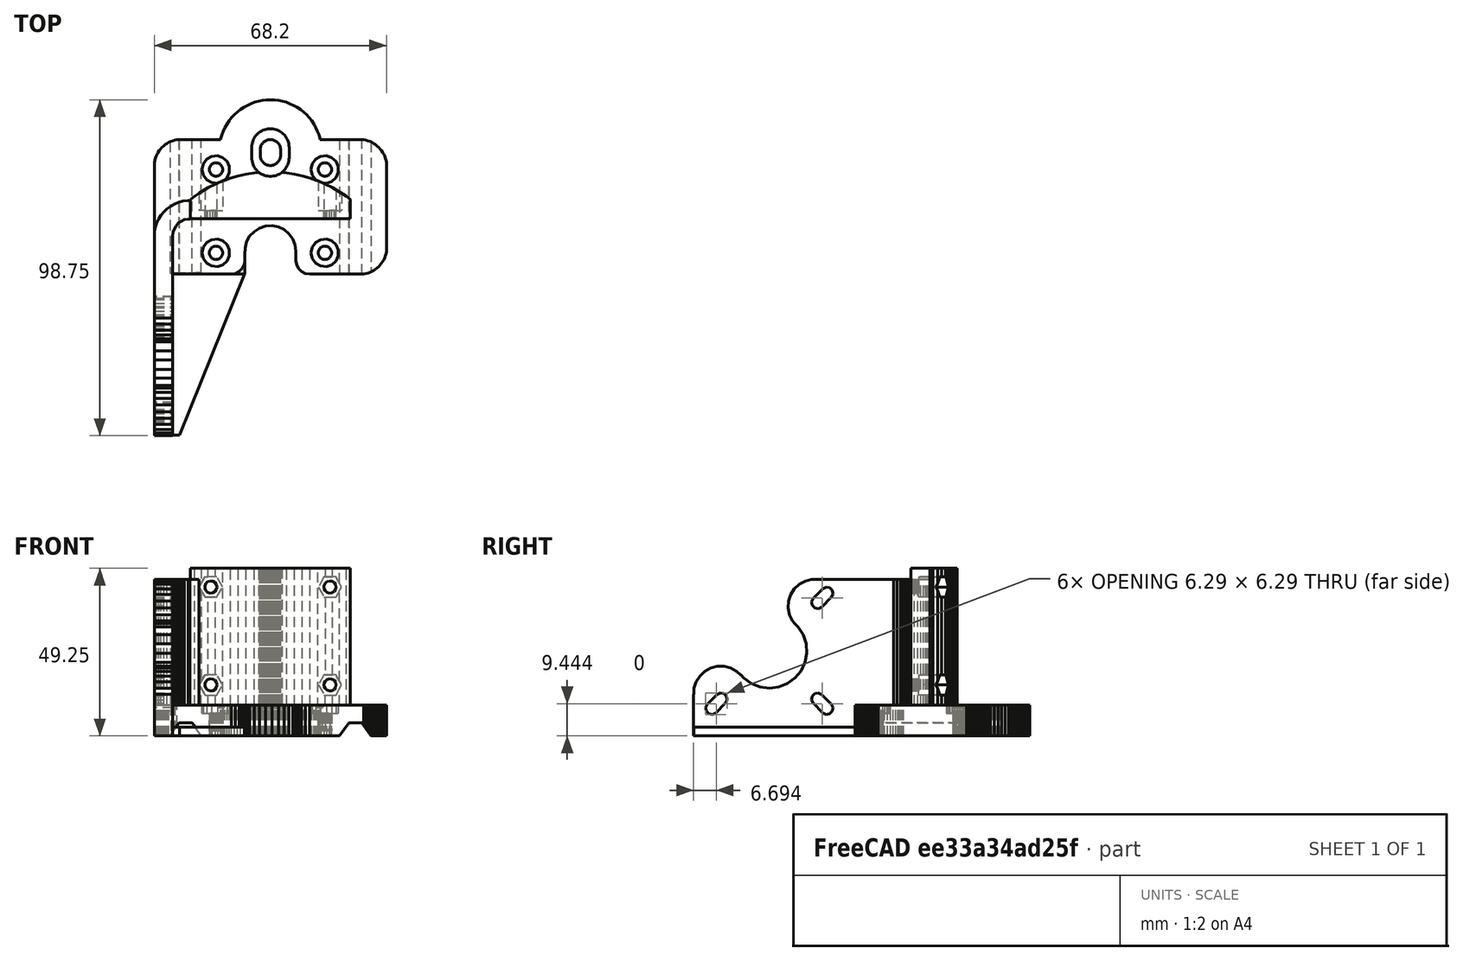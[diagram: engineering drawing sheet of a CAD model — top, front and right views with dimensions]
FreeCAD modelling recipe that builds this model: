
FCSTD DOCUMENT  (FreeCAD 0.15R4619 (Git))
Label: x_end_motor_M5
License: All rights reserved
LicenseURL: http://en.wikipedia.org/wiki/All_rights_reserved
objects: Part::Feature×1, Sketcher::SketchObject×1, PartDesign::Pad×1
note: 4 computed .brp shape members not serialized (recipe doc carries the construction recipe); baked Part::Feature solids carry a one-line shape summary decoded from their .brp

FEATURE [Part::Feature] Solid
  shape: bbox 68.2 x 98.75 x 49.25 mm, 1015 faces (baked)
FEATURE [Sketcher::SketchObject] Sketch
  ExternalGeometry = -> [Solid]
  Placement = pos=(0,0,-4.5) rot=(1,0,0;3.14159rad)
  Support = -> Solid [Face265]
  sketch-geometry (11):
    g0: LineSegment [constr] StartX=-5.5 StartY=-11.5 StartZ=0 EndX=5.5 EndY=-14.5 EndZ=0
    g1: LineSegment [constr] StartX=5.5 StartY=-11.5 StartZ=0 EndX=-5.5 EndY=-14.5 EndZ=0
    g2: LineSegment StartX=-3 StartY=-12.1818 StartZ=0 EndX=-3 EndY=-13.8182 EndZ=0
    g3: LineSegment StartX=3 StartY=-12.1818 StartZ=0 EndX=3 EndY=-13.8182 EndZ=0
    g4: LineSegment [constr] StartX=0 StartY=-12.1818 StartZ=0 EndX=0 EndY=-13 EndZ=0
    g5: LineSegment [constr] StartX=0 StartY=-13 StartZ=0 EndX=0 EndY=-13.8182 EndZ=0
    g6: LineSegment [constr] StartX=-3 StartY=-12.1818 StartZ=0 EndX=3 EndY=-12.1818 EndZ=0
    g7: LineSegment [constr] StartX=-3 StartY=-13.8182 StartZ=0 EndX=3 EndY=-13.8182 EndZ=0
    g8: ArcOfCircle CenterX=0 CenterY=-12.1818 CenterZ=0 NormalX=0 NormalY=0 NormalZ=1 Radius=3 StartAngle=0 EndAngle=3.14159
    g9: ArcOfCircle CenterX=0 CenterY=-13.8182 CenterZ=0 NormalX=0 NormalY=0 NormalZ=1 Radius=3 StartAngle=3.14159 EndAngle=6.28319
    g10: Circle CenterX=0 CenterY=-13 CenterZ=0 NormalX=0 NormalY=0 NormalZ=1 Radius=7.27781
  constraints (30):
    c: Coincident(g0,g-3)
    c: Coincident(g0,g-5)
    c: Coincident(g1,g-4)
    c: Coincident(g1,g-6)
    c: PointOnObject(g2,g0)
    c: PointOnObject(g2,g1)
    c: PointOnObject(g3,g1)
    c: PointOnObject(g3,g0)
    c: Vertical(g3)
    c: PointOnObject(g4,g1)
    c: Vertical(g4)
    c: Coincident(g4,g5)
    c: Vertical(g5)
    c: Vertical(g2)
    c: PointOnObject(g4,g0)
    c: Equal(g4,g5)
    c: Coincident(g6,g2)
    c: Coincident(g6,g3)
    c: Horizontal(g6)
    c: Coincident(g7,g2)
    c: Coincident(g7,g3)
    c: PointOnObject(g5,g7)
    c: Coincident(g8,g4)
    c: Coincident(g8,g3)
    c: Coincident(g8,g2)
    c: Coincident(g9,g5)
    c: Coincident(g9,g3)
    c: Coincident(g9,g2)
    c: Radius(g8) = 3
    c: Coincident(g10,g4)
FEATURE [PartDesign::Pad] Pad
  Length = 8
  Length2 = 100
  Reversed = true
  Sketch = -> Sketch
  Type = 0
